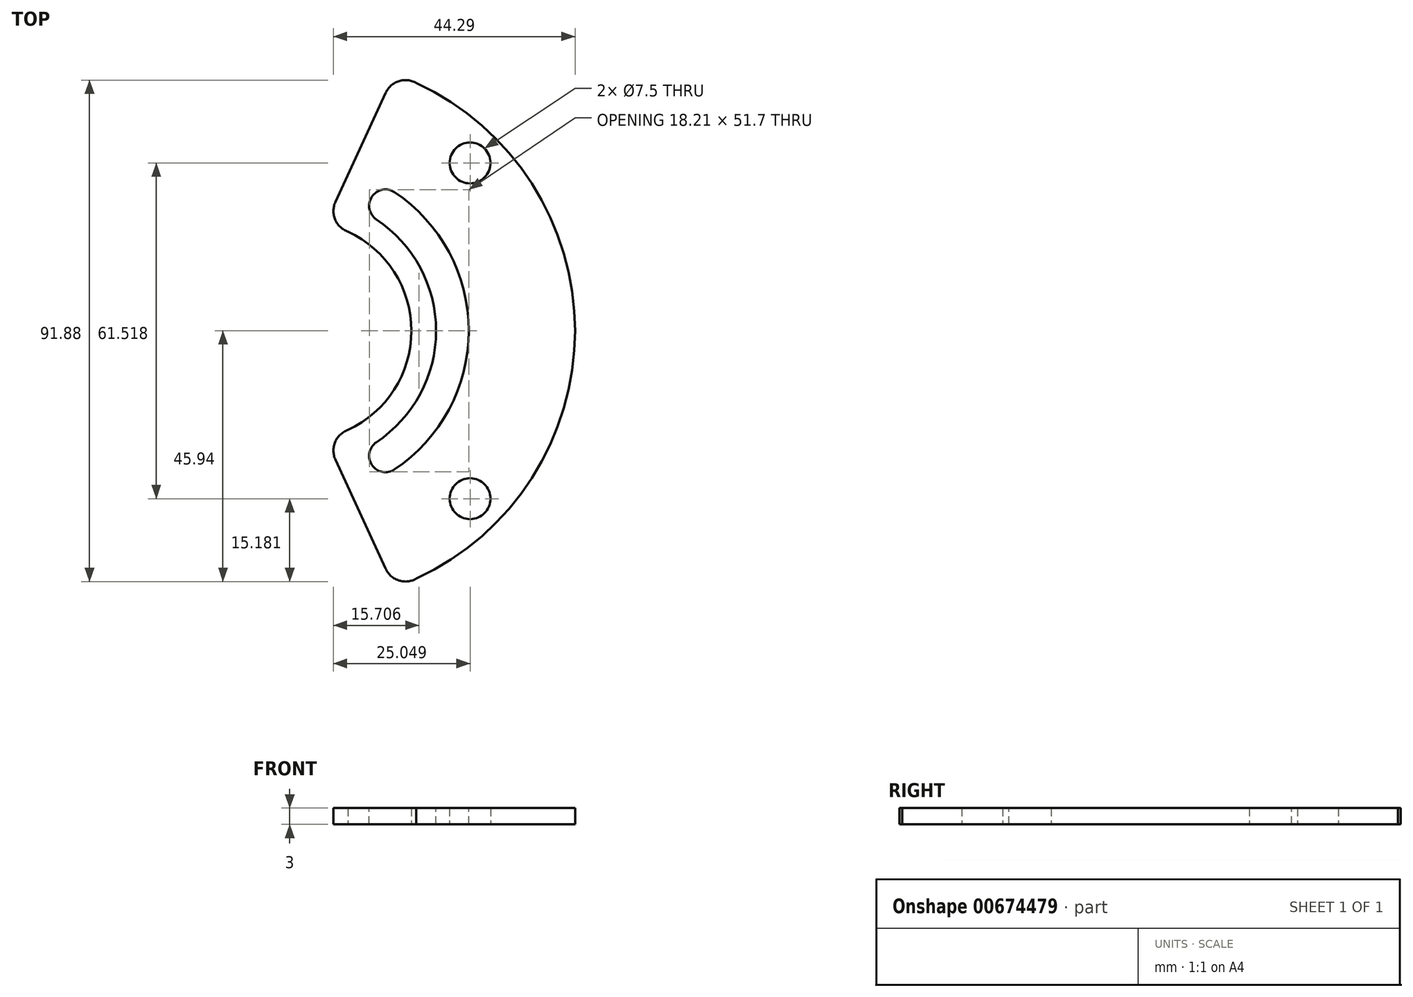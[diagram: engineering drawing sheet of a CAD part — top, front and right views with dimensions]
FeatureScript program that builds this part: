
annotation { "Feature Type Name" : "Feature", "Feature Type Description" : "" }
export const myFeature = defineFeature(function(context is Context, id is Id, definition is map)
    precondition{}
    {
        {
            var Q0;
            Q0=qCreatedBy(makeId("Top.planeOp"),FACE);
            var sketch = newSketch(context, id + "F0", { "sketchPlane" : qUnion([Q0])});
            skCircle(sketch, "E0", {"center": v(0, 0) * mm, "radius": 43.5 * mm, "construction": true});
            skLineSegment(sketch, "E1", {"start": v(0, 0) * mm, "end": v(30.76, 30.76) * mm, "construction": true});
            skCircle(sketch, "E2", {"center": v(30.76, 30.76) * mm, "radius": 3.75 * mm});
            skCircle(sketch, "E3.1.0", {"center": v(-30.76, 30.76) * mm, "radius": 3.75 * mm});
            skCircle(sketch, "E3.2.0", {"center": v(-30.76, -30.76) * mm, "radius": 3.75 * mm});
            skCircle(sketch, "E3.3.0", {"center": v(30.76, -30.76) * mm, "radius": 3.75 * mm});
            skLineSegment(sketch, "E4", {"start": v(0, 0) * mm, "end": v(30.76, -30.76) * mm, "construction": true});
            skSolve(sketch);
        }
        {
            var Q0;
            Q0=qCreatedBy(makeId("Top.planeOp"),FACE);
            var sketch = newSketch(context, id + "F1", { "sketchPlane" : qUnion([Q0])});
            skLineSegment(sketch, "E5", {"start": v(6.08, 23.6) * mm, "end": v(15.3, 43.61) * mm});
            skLineSegment(sketch, "E6", {"start": v(6.08, -23.6) * mm, "end": v(15.3, -43.61) * mm});
            skLineSegment(sketch, "E7", {"start": v(0, 0) * mm, "end": v(0, 47.02) * mm, "construction": true});
            skLineSegment(sketch, "E8", {"start": v(0, 0) * mm, "end": v(0, -46.33) * mm, "construction": true});
            skPoint(sketch, "E9.visualSharp", {"position": v(16.58, 46.4) * mm});
            skArc(sketch, "E9.filletArc", {"start": v(20.9, 45.42) * mm, "mid": v(17.7, 45.75) * mm, "end": v(15.3, 43.61) * mm});
            skPoint(sketch, "E10.visualSharp", {"position": v(3.88, 18.83) * mm});
            skArc(sketch, "E10.filletArc", {"start": v(6.08, 23.6) * mm, "mid": v(6.02, 20.4) * mm, "end": v(8.35, 18.17) * mm});
            skPoint(sketch, "E11.visualSharp", {"position": v(3.88, -18.83) * mm});
            skArc(sketch, "E11.filletArc", {"start": v(8.35, -18.17) * mm, "mid": v(6.02, -20.4) * mm, "end": v(6.08, -23.6) * mm});
            skPoint(sketch, "E12.visualSharp", {"position": v(16.58, -46.4) * mm});
            skArc(sketch, "E12.filletArc", {"start": v(15.3, -43.61) * mm, "mid": v(17.7, -45.75) * mm, "end": v(20.9, -45.42) * mm});
            skLineSegment(sketch, "E13", {"start": v(0, 0) * mm, "end": v(50, 0) * mm, "construction": true});
            skArc(sketch, "E14", {"start": v(8.35, 18.17) * mm, "mid": v(20, 0) * mm, "end": v(8.35, -18.17) * mm});
            skArc(sketch, "E15", {"start": v(20.9, 45.42) * mm, "mid": v(50, 0) * mm, "end": v(20.9, -45.42) * mm});
            skLineSegment(sketch, "E16", {"start": v(20.9, 45.42) * mm, "end": v(20.9, 0) * mm, "construction": true});
            skLineSegment(sketch, "E17", {"start": v(20.9, 0) * mm, "end": v(20.9, -45.42) * mm, "construction": true});
            skLineSegment(sketch, "E18", {"start": v(0, 43.61) * mm, "end": v(15.3, 43.61) * mm, "construction": true});
            skLineSegment(sketch, "E19", {"start": v(0, -43.61) * mm, "end": v(15.3, -43.61) * mm, "construction": true});
            skSolve(sketch);
        }
        {
            var Q0;
            Q0=makeQuery(id+"F1.imprint","IMPRINT",FACE,{"disambiguationData":[TD([[makeQuery(id+"F1.imprint","IMPRINT",EDGE,{"derivedFrom":sQuery(id+"F1.wireOp",EDGE,"E5")}),-1.0]])]});
            extrude(context, id + "F2", {"entities" : qUnion([Q0]), "depth" : 3 * mm, "offsetDistance" : 25 * mm});
        }
        {
            var Q0;
            Q0=makeQuery(id+"F0.imprint","IMPRINT",FACE,{"disambiguationData":[TD([[makeQuery(id+"F0.imprint","IMPRINT",EDGE,{"derivedFrom":sQuery(id+"F0.wireOp",EDGE,"E2")}),1.0]])]});
            var Q1;
            Q1=makeQuery(id+"F0.imprint","IMPRINT",FACE,{"disambiguationData":[TD([[makeQuery(id+"F0.imprint","IMPRINT",EDGE,{"derivedFrom":sQuery(id+"F0.wireOp",EDGE,"E3.3.0")}),1.0]])]});
            extrude(context, id + "F3", {"entities" : qUnion([Q0, Q1]), "operationType" : NewBodyOperationType.REMOVE, "depth" : 25 * mm, "offsetDistance" : 25 * mm});
        }
        {
            var Q0;
            Q0=makeQuery(id+"F2.opExtrude","CAP_FACE",FACE,{"disambiguationData":[OSD([sQuery(id+"F1.wireOp",EDGE,"KiuFZQME-wWnU-ktu5-Gd9x-qji5TMNZz2fd"),sQuery(id+"F1.wireOp",EDGE,"G5eraXv0-ftC7-V2Hx-4i3N-1R2XA50WnSdq"),sQuery(id+"F1.wireOp",EDGE,"E5"),sQuery(id+"F1.wireOp",EDGE,"E6"),sQuery(id+"F1.wireOp",EDGE,"57560024-62e8-479f-91f4-8b403f4d0ad7.filletArc"),sQuery(id+"F1.wireOp",EDGE,"ddf71622-e854-4fa8-aca5-087326283111.filletArc"),sQuery(id+"F1.wireOp",EDGE,"85b82a5b-4425-4996-801d-5779b438c59f.filletArc"),sQuery(id+"F1.wireOp",EDGE,"35c327b1-5974-4460-b54d-dc77ba413df5.filletArc")])],"isStart":false});
            var sketch = newSketch(context, id + "F4", { "sketchPlane" : qUnion([Q0])});
            skArc(sketch, "E20", {"start": v(13.6, 20.4) * mm, "mid": v(24.52, 0) * mm, "end": v(13.6, -20.4) * mm});
            skArc(sketch, "E21", {"start": v(16.92, 25.4) * mm, "mid": v(30.52, 0) * mm, "end": v(16.92, -25.4) * mm});
            skLineSegment(sketch, "E22", {"start": v(0, 0) * mm, "end": v(16.92, -25.4) * mm, "construction": true});
            skLineSegment(sketch, "E23", {"start": v(0, 0) * mm, "end": v(16.92, 25.4) * mm, "construction": true});
            skLineSegment(sketch, "E24", {"start": v(13.6, 20.4) * mm, "end": v(13.6, 0) * mm, "construction": true});
            skLineSegment(sketch, "E25", {"start": v(13.6, 0) * mm, "end": v(13.6, -20.4) * mm, "construction": true});
            skArc(sketch, "E26", {"start": v(13.6, 20.4) * mm, "mid": v(12.76, 24.57) * mm, "end": v(16.92, 25.4) * mm});
            skArc(sketch, "E27", {"start": v(13.6, -20.4) * mm, "mid": v(12.76, -24.57) * mm, "end": v(16.92, -25.4) * mm});
            skSolve(sketch);
        }
        {
            var Q0;
            Q0=qSketchRegion(id+"F4",true);
            extrude(context, id + "F5", {"entities" : qUnion([Q0]), "operationType" : NewBodyOperationType.REMOVE, "oppositeDirection" : true, "depth" : 25 * mm, "offsetDistance" : 25 * mm});
        }
    });
